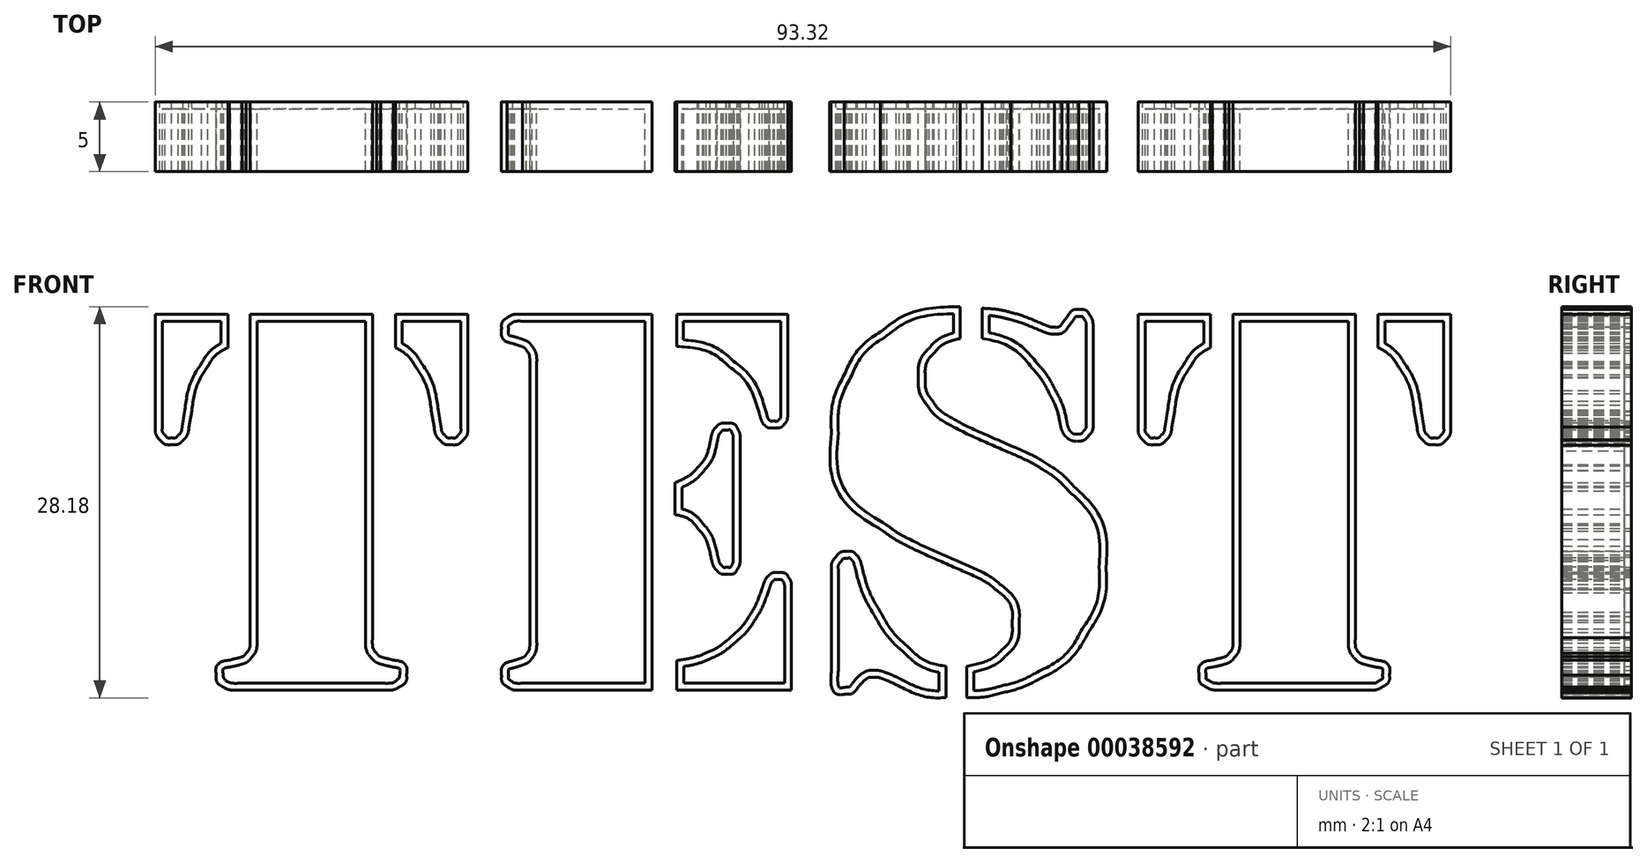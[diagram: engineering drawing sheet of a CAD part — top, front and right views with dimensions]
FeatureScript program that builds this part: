
annotation { "Feature Type Name" : "Feature", "Feature Type Description" : "" }
export const myFeature = defineFeature(function(context is Context, id is Id, definition is map)
    precondition{}
    {
        {
            var Q0;
            Q0=qCreatedBy(makeId("Front.planeOp"),FACE);
            var sketch = newSketch(context, id + "F0", { "sketchPlane" : qUnion([Q0])});
            skLineSegment(sketch, "E0", {"start": v(-31.02, 13.54) * mm, "end": v(-31.02, -9.77) * mm});
            skFitSpline(sketch, "E1", {"points": [v(-31.02, -9.77) * mm, v(-31.02, -10.29) * mm, v(-30.92, -10.66) * mm, v(-30.72, -10.88) * mm]});
            skFitSpline(sketch, "E2", {"points": [v(-30.72, -10.88) * mm, v(-30.61, -11.02) * mm, v(-30.51, -11.1) * mm, v(-30.42, -11.13) * mm]});
            skFitSpline(sketch, "E3", {"points": [v(-30.42, -11.13) * mm, v(-30.33, -11.17) * mm, v(-30.02, -11.25) * mm, v(-29.5, -11.38) * mm]});
            skFitSpline(sketch, "E4", {"points": [v(-29.5, -11.38) * mm, v(-28.87, -11.53) * mm, v(-28.56, -11.89) * mm, v(-28.56, -12.47) * mm]});
            skFitSpline(sketch, "E5", {"points": [v(-28.56, -12.47) * mm, v(-28.56, -12.82) * mm, v(-28.73, -13.1) * mm, v(-29.07, -13.3) * mm]});
            skFitSpline(sketch, "E6", {"points": [v(-29.07, -13.3) * mm, v(-29.32, -13.46) * mm, v(-29.75, -13.54) * mm, v(-30.34, -13.54) * mm]});
            skLineSegment(sketch, "E7", {"start": v(-30.34, -13.54) * mm, "end": v(-31, -13.54) * mm});
            skLineSegment(sketch, "E8", {"start": v(-31, -13.54) * mm, "end": v(-39.85, -13.54) * mm});
            skLineSegment(sketch, "E9", {"start": v(-39.85, -13.54) * mm, "end": v(-40.5, -13.54) * mm});
            skFitSpline(sketch, "E10", {"points": [v(-40.5, -13.54) * mm, v(-41.08, -13.54) * mm, v(-41.52, -13.45) * mm, v(-41.82, -13.28) * mm]});
            skFitSpline(sketch, "E11", {"points": [v(-41.82, -13.28) * mm, v(-42.12, -13.1) * mm, v(-42.27, -12.83) * mm, v(-42.27, -12.47) * mm]});
            skFitSpline(sketch, "E12", {"points": [v(-42.27, -12.47) * mm, v(-42.27, -11.89) * mm, v(-41.95, -11.53) * mm, v(-41.31, -11.38) * mm]});
            skFitSpline(sketch, "E13", {"points": [v(-41.31, -11.38) * mm, v(-40.8, -11.25) * mm, v(-40.5, -11.17) * mm, v(-40.4, -11.13) * mm]});
            skFitSpline(sketch, "E14", {"points": [v(-40.4, -11.13) * mm, v(-40.3, -11.1) * mm, v(-40.22, -11.02) * mm, v(-40.12, -10.88) * mm]});
            skFitSpline(sketch, "E15", {"points": [v(-40.12, -10.88) * mm, v(-39.93, -10.66) * mm, v(-39.83, -10.29) * mm, v(-39.83, -9.77) * mm]});
            skLineSegment(sketch, "E16", {"start": v(-39.83, -9.77) * mm, "end": v(-39.83, 13.54) * mm});
            skLineSegment(sketch, "E17", {"start": v(-39.83, 13.54) * mm, "end": v(-31.02, 13.54) * mm});
            skLineSegment(sketch, "E18", {"start": v(-24.15, 13.54) * mm, "end": v(-24.15, 5.43) * mm});
            skFitSpline(sketch, "E19", {"points": [v(-24.15, 5.43) * mm, v(-24.15, 5.04) * mm, v(-24.26, 4.73) * mm, v(-24.48, 4.5) * mm]});
            skFitSpline(sketch, "E20", {"points": [v(-24.48, 4.5) * mm, v(-24.7, 4.26) * mm, v(-24.98, 4.14) * mm, v(-25.32, 4.14) * mm]});
            skFitSpline(sketch, "E21", {"points": [v(-25.32, 4.14) * mm, v(-25.65, 4.14) * mm, v(-25.93, 4.25) * mm, v(-26.14, 4.46) * mm]});
            skFitSpline(sketch, "E22", {"points": [v(-26.14, 4.46) * mm, v(-26.36, 4.68) * mm, v(-26.5, 4.98) * mm, v(-26.57, 5.37) * mm]});
            skLineSegment(sketch, "E23", {"start": v(-26.57, 5.37) * mm, "end": v(-26.77, 6.58) * mm});
            skFitSpline(sketch, "E24", {"points": [v(-26.77, 6.58) * mm, v(-26.97, 7.8) * mm, v(-27.35, 8.87) * mm, v(-27.92, 9.77) * mm]});
            skFitSpline(sketch, "E25", {"points": [v(-27.92, 9.77) * mm, v(-28.28, 10.33) * mm, v(-28.76, 10.79) * mm, v(-29.37, 11.14) * mm]});
            skLineSegment(sketch, "E26", {"start": v(-29.37, 11.14) * mm, "end": v(-29.37, 13.54) * mm});
            skLineSegment(sketch, "E27", {"start": v(-29.37, 13.54) * mm, "end": v(-24.15, 13.54) * mm});
            skLineSegment(sketch, "E28", {"start": v(-46.65, 13.54) * mm, "end": v(-41.43, 13.54) * mm});
            skLineSegment(sketch, "E29", {"start": v(-41.43, 13.54) * mm, "end": v(-41.43, 11.14) * mm});
            skFitSpline(sketch, "E30", {"points": [v(-41.43, 11.14) * mm, v(-42.06, 10.79) * mm, v(-42.54, 10.33) * mm, v(-42.88, 9.77) * mm]});
            skFitSpline(sketch, "E31", {"points": [v(-42.88, 9.77) * mm, v(-43.45, 8.87) * mm, v(-43.83, 7.8) * mm, v(-44.03, 6.58) * mm]});
            skLineSegment(sketch, "E32", {"start": v(-44.03, 6.58) * mm, "end": v(-44.23, 5.37) * mm});
            skFitSpline(sketch, "E33", {"points": [v(-44.23, 5.37) * mm, v(-44.3, 4.98) * mm, v(-44.44, 4.68) * mm, v(-44.66, 4.46) * mm]});
            skFitSpline(sketch, "E34", {"points": [v(-44.66, 4.46) * mm, v(-44.88, 4.25) * mm, v(-45.15, 4.14) * mm, v(-45.48, 4.14) * mm]});
            skFitSpline(sketch, "E35", {"points": [v(-45.48, 4.14) * mm, v(-45.83, 4.14) * mm, v(-46.1, 4.26) * mm, v(-46.33, 4.5) * mm]});
            skFitSpline(sketch, "E36", {"points": [v(-46.33, 4.5) * mm, v(-46.54, 4.73) * mm, v(-46.65, 5.04) * mm, v(-46.65, 5.43) * mm]});
            skLineSegment(sketch, "E37", {"start": v(-46.65, 5.43) * mm, "end": v(-46.65, 13.54) * mm});
            skLineSegment(sketch, "E38", {"start": v(-10.87, 13.54) * mm, "end": v(-10.87, -13.54) * mm});
            skLineSegment(sketch, "E39", {"start": v(-10.87, -13.54) * mm, "end": v(-19.7, -13.54) * mm});
            skLineSegment(sketch, "E40", {"start": v(-19.7, -13.54) * mm, "end": v(-20.22, -13.54) * mm});
            skFitSpline(sketch, "E41", {"points": [v(-20.22, -13.54) * mm, v(-20.7, -13.54) * mm, v(-21.06, -13.45) * mm, v(-21.32, -13.28) * mm]});
            skFitSpline(sketch, "E42", {"points": [v(-21.32, -13.28) * mm, v(-21.58, -13.1) * mm, v(-21.7, -12.84) * mm, v(-21.7, -12.51) * mm]});
            skFitSpline(sketch, "E43", {"points": [v(-21.7, -12.51) * mm, v(-21.7, -11.97) * mm, v(-21.44, -11.61) * mm, v(-20.92, -11.44) * mm]});
            skFitSpline(sketch, "E44", {"points": [v(-20.92, -11.44) * mm, v(-20.48, -11.3) * mm, v(-20.22, -11.2) * mm, v(-20.15, -11.17) * mm]});
            skFitSpline(sketch, "E45", {"points": [v(-20.15, -11.17) * mm, v(-20.08, -11.14) * mm, v(-20, -11.06) * mm, v(-19.92, -10.94) * mm]});
            skFitSpline(sketch, "E46", {"points": [v(-19.92, -10.94) * mm, v(-19.76, -10.73) * mm, v(-19.69, -10.4) * mm, v(-19.68, -9.93) * mm]});
            skLineSegment(sketch, "E47", {"start": v(-19.68, -9.93) * mm, "end": v(-19.68, 9.93) * mm});
            skFitSpline(sketch, "E48", {"points": [v(-19.68, 9.93) * mm, v(-19.69, 10.4) * mm, v(-19.76, 10.73) * mm, v(-19.92, 10.94) * mm]});
            skFitSpline(sketch, "E49", {"points": [v(-19.92, 10.94) * mm, v(-20, 11.06) * mm, v(-20.08, 11.14) * mm, v(-20.15, 11.17) * mm]});
            skFitSpline(sketch, "E50", {"points": [v(-20.15, 11.17) * mm, v(-20.22, 11.2) * mm, v(-20.48, 11.3) * mm, v(-20.92, 11.44) * mm]});
            skFitSpline(sketch, "E51", {"points": [v(-20.92, 11.44) * mm, v(-21.44, 11.61) * mm, v(-21.7, 11.97) * mm, v(-21.7, 12.51) * mm]});
            skFitSpline(sketch, "E52", {"points": [v(-21.7, 12.51) * mm, v(-21.7, 12.84) * mm, v(-21.58, 13.1) * mm, v(-21.32, 13.28) * mm]});
            skFitSpline(sketch, "E53", {"points": [v(-21.32, 13.28) * mm, v(-21.06, 13.45) * mm, v(-20.7, 13.54) * mm, v(-20.22, 13.54) * mm]});
            skLineSegment(sketch, "E54", {"start": v(-20.22, 13.54) * mm, "end": v(-19.7, 13.54) * mm});
            skLineSegment(sketch, "E55", {"start": v(-19.7, 13.54) * mm, "end": v(-10.87, 13.54) * mm});
            skLineSegment(sketch, "E56", {"start": v(-9.1, 13.54) * mm, "end": v(-1.11, 13.54) * mm});
            skLineSegment(sketch, "E57", {"start": v(-1.11, 13.54) * mm, "end": v(-1.11, 6.52) * mm});
            skFitSpline(sketch, "E58", {"points": [v(-1.11, 6.52) * mm, v(-1.11, 6.1) * mm, v(-1.2, 5.81) * mm, v(-1.35, 5.63) * mm]});
            skFitSpline(sketch, "E59", {"points": [v(-1.35, 5.63) * mm, v(-1.5, 5.44) * mm, v(-1.76, 5.35) * mm, v(-2.1, 5.35) * mm]});
            skFitSpline(sketch, "E60", {"points": [v(-2.1, 5.35) * mm, v(-2.4, 5.35) * mm, v(-2.6, 5.4) * mm, v(-2.74, 5.53) * mm]});
            skFitSpline(sketch, "E61", {"points": [v(-2.74, 5.53) * mm, v(-2.87, 5.65) * mm, v(-3, 5.9) * mm, v(-3.12, 6.26) * mm]});
            skFitSpline(sketch, "E62", {"points": [v(-3.12, 6.26) * mm, v(-3.62, 7.8) * mm, v(-4.36, 8.97) * mm, v(-5.33, 9.77) * mm]});
            skFitSpline(sketch, "E63", {"points": [v(-5.33, 9.77) * mm, v(-6.3, 10.58) * mm, v(-7.56, 11.06) * mm, v(-9.1, 11.22) * mm]});
            skLineSegment(sketch, "E64", {"start": v(-9.1, 11.22) * mm, "end": v(-9.1, 13.54) * mm});
            skLineSegment(sketch, "E65", {"start": v(-9.2, -0.9) * mm, "end": v(-9.2, 1.4) * mm});
            skFitSpline(sketch, "E66", {"points": [v(-9.2, 1.4) * mm, v(-8.44, 1.77) * mm, v(-7.87, 2.17) * mm, v(-7.5, 2.6) * mm]});
            skFitSpline(sketch, "E67", {"points": [v(-7.5, 2.6) * mm, v(-7.13, 3.05) * mm, v(-6.86, 3.63) * mm, v(-6.69, 4.36) * mm]});
            skFitSpline(sketch, "E68", {"points": [v(-6.69, 4.36) * mm, v(-6.58, 4.86) * mm, v(-6.44, 5.2) * mm, v(-6.27, 5.4) * mm]});
            skFitSpline(sketch, "E69", {"points": [v(-6.27, 5.4) * mm, v(-6.1, 5.59) * mm, v(-5.85, 5.69) * mm, v(-5.54, 5.69) * mm]});
            skFitSpline(sketch, "E70", {"points": [v(-5.54, 5.69) * mm, v(-5.11, 5.69) * mm, v(-4.82, 5.52) * mm, v(-4.66, 5.19) * mm]});
            skFitSpline(sketch, "E71", {"points": [v(-4.66, 5.19) * mm, v(-4.57, 5.02) * mm, v(-4.52, 4.63) * mm, v(-4.52, 4.02) * mm]});
            skLineSegment(sketch, "E72", {"start": v(-4.52, 4.02) * mm, "end": v(-4.52, -3.54) * mm});
            skFitSpline(sketch, "E73", {"points": [v(-4.52, -3.54) * mm, v(-4.52, -4.16) * mm, v(-4.6, -4.6) * mm, v(-4.73, -4.83) * mm]});
            skFitSpline(sketch, "E74", {"points": [v(-4.73, -4.83) * mm, v(-4.87, -5.07) * mm, v(-5.13, -5.19) * mm, v(-5.5, -5.19) * mm]});
            skFitSpline(sketch, "E75", {"points": [v(-5.5, -5.19) * mm, v(-5.8, -5.19) * mm, v(-6.04, -5.1) * mm, v(-6.21, -4.91) * mm]});
            skFitSpline(sketch, "E76", {"points": [v(-6.21, -4.91) * mm, v(-6.38, -4.73) * mm, v(-6.52, -4.42) * mm, v(-6.63, -3.98) * mm]});
            skFitSpline(sketch, "E77", {"points": [v(-6.63, -3.98) * mm, v(-6.85, -3.07) * mm, v(-7.17, -2.36) * mm, v(-7.6, -1.88) * mm]});
            skFitSpline(sketch, "E78", {"points": [v(-7.6, -1.88) * mm, v(-8, -1.39) * mm, v(-8.55, -1.06) * mm, v(-9.2, -0.9) * mm]});
            skLineSegment(sketch, "E79", {"start": v(-9.09, -13.54) * mm, "end": v(-9.09, -11.4) * mm});
            skFitSpline(sketch, "E80", {"points": [v(-9.09, -11.4) * mm, v(-8.23, -11.27) * mm, v(-7.52, -11.08) * mm, v(-6.96, -10.84) * mm]});
            skFitSpline(sketch, "E81", {"points": [v(-6.96, -10.84) * mm, v(-6.4, -10.6) * mm, v(-5.83, -10.24) * mm, v(-5.26, -9.75) * mm]});
            skFitSpline(sketch, "E82", {"points": [v(-5.26, -9.75) * mm, v(-4.69, -9.26) * mm, v(-4.24, -8.76) * mm, v(-3.9, -8.24) * mm]});
            skFitSpline(sketch, "E83", {"points": [v(-3.9, -8.24) * mm, v(-3.56, -7.71) * mm, v(-3.24, -7.02) * mm, v(-2.94, -6.16) * mm]});
            skFitSpline(sketch, "E84", {"points": [v(-2.94, -6.16) * mm, v(-2.8, -5.74) * mm, v(-2.64, -5.45) * mm, v(-2.48, -5.3) * mm]});
            skFitSpline(sketch, "E85", {"points": [v(-2.48, -5.3) * mm, v(-2.32, -5.15) * mm, v(-2.1, -5.07) * mm, v(-1.83, -5.07) * mm]});
            skFitSpline(sketch, "E86", {"points": [v(-1.83, -5.07) * mm, v(-1.46, -5.07) * mm, v(-1.2, -5.18) * mm, v(-1.05, -5.4) * mm]});
            skFitSpline(sketch, "E87", {"points": [v(-1.05, -5.4) * mm, v(-0.9, -5.62) * mm, v(-0.83, -6) * mm, v(-0.83, -6.54) * mm]});
            skLineSegment(sketch, "E88", {"start": v(-0.83, -6.54) * mm, "end": v(-0.83, -13.54) * mm});
            skLineSegment(sketch, "E89", {"start": v(-0.83, -13.54) * mm, "end": v(-9.09, -13.54) * mm});
            skLineSegment(sketch, "E90", {"start": v(11.33, 14.08) * mm, "end": v(11.33, 11.8) * mm});
            skFitSpline(sketch, "E91", {"points": [v(11.33, 11.8) * mm, v(10.51, 11.57) * mm, v(9.89, 11.22) * mm, v(9.46, 10.76) * mm]});
            skFitSpline(sketch, "E92", {"points": [v(9.46, 10.76) * mm, v(9.03, 10.29) * mm, v(8.81, 9.7) * mm, v(8.81, 9.02) * mm]});
            skFitSpline(sketch, "E93", {"points": [v(8.81, 9.02) * mm, v(8.81, 8.36) * mm, v(8.99, 7.78) * mm, v(9.35, 7.28) * mm]});
            skFitSpline(sketch, "E94", {"points": [v(9.35, 7.28) * mm, v(9.7, 6.79) * mm, v(10.29, 6.31) * mm, v(11.1, 5.86) * mm]});
            skFitSpline(sketch, "E95", {"points": [v(11.1, 5.86) * mm, v(11.65, 5.56) * mm, v(12.9, 4.98) * mm, v(14.86, 4.12) * mm]});
            skFitSpline(sketch, "E96", {"points": [v(14.86, 4.12) * mm, v(16.05, 3.6) * mm, v(16.98, 3.14) * mm, v(17.63, 2.72) * mm]});
            skFitSpline(sketch, "E97", {"points": [v(17.63, 2.72) * mm, v(18.29, 2.3) * mm, v(18.9, 1.78) * mm, v(19.49, 1.16) * mm]});
            skFitSpline(sketch, "E98", {"points": [v(19.49, 1.16) * mm, v(21.05, -0.48) * mm, v(21.83, -2.43) * mm, v(21.83, -4.7) * mm]});
            skFitSpline(sketch, "E99", {"points": [v(21.83, -4.7) * mm, v(21.83, -6.4) * mm, v(21.4, -7.96) * mm, v(20.56, -9.38) * mm]});
            skFitSpline(sketch, "E100", {"points": [v(20.56, -9.38) * mm, v(19.71, -10.8) * mm, v(18.55, -11.9) * mm, v(17.07, -12.7) * mm]});
            skFitSpline(sketch, "E101", {"points": [v(17.07, -12.7) * mm, v(16.27, -13.13) * mm, v(15.4, -13.47) * mm, v(14.46, -13.71) * mm]});
            skFitSpline(sketch, "E102", {"points": [v(14.46, -13.71) * mm, v(13.51, -13.96) * mm, v(12.63, -14.08) * mm, v(11.8, -14.08) * mm]});
            skLineSegment(sketch, "E103", {"start": v(11.8, -14.08) * mm, "end": v(11.8, -11.82) * mm});
            skFitSpline(sketch, "E104", {"points": [v(11.8, -11.82) * mm, v(12.96, -11.54) * mm, v(13.79, -11.15) * mm, v(14.3, -10.66) * mm]});
            skFitSpline(sketch, "E105", {"points": [v(14.3, -10.66) * mm, v(14.8, -10.16) * mm, v(15.06, -9.49) * mm, v(15.06, -8.64) * mm]});
            skFitSpline(sketch, "E106", {"points": [v(15.06, -8.64) * mm, v(15.06, -7.76) * mm, v(14.66, -6.98) * mm, v(13.87, -6.3) * mm]});
            skFitSpline(sketch, "E107", {"points": [v(13.87, -6.3) * mm, v(13.34, -5.86) * mm, v(12.34, -5.32) * mm, v(10.85, -4.67) * mm]});
            skFitSpline(sketch, "E108", {"points": [v(10.85, -4.67) * mm, v(9.23, -3.96) * mm, v(8.11, -3.45) * mm, v(7.51, -3.15) * mm]});
            skFitSpline(sketch, "E109", {"points": [v(7.51, -3.15) * mm, v(6.9, -2.84) * mm, v(6.33, -2.48) * mm, v(5.77, -2.07) * mm]});
            skFitSpline(sketch, "E110", {"points": [v(5.77, -2.07) * mm, v(3.29, -0.3) * mm, v(2.04, 2.06) * mm, v(2.04, 5.01) * mm]});
            skFitSpline(sketch, "E111", {"points": [v(2.04, 5.01) * mm, v(2.04, 6.52) * mm, v(2.35, 7.91) * mm, v(2.98, 9.19) * mm]});
            skFitSpline(sketch, "E112", {"points": [v(2.98, 9.19) * mm, v(3.6, 10.46) * mm, v(4.46, 11.5) * mm, v(5.58, 12.27) * mm]});
            skFitSpline(sketch, "E113", {"points": [v(5.58, 12.27) * mm, v(7.12, 13.36) * mm, v(9.04, 13.96) * mm, v(11.33, 14.08) * mm]});
            skLineSegment(sketch, "E114", {"start": v(12.9, 11.8) * mm, "end": v(12.9, 13.98) * mm});
            skFitSpline(sketch, "E115", {"points": [v(12.9, 13.98) * mm, v(13.7, 13.93) * mm, v(14.38, 13.82) * mm, v(14.96, 13.67) * mm]});
            skFitSpline(sketch, "E116", {"points": [v(14.96, 13.67) * mm, v(15.54, 13.52) * mm, v(16.37, 13.22) * mm, v(17.44, 12.77) * mm]});
            skFitSpline(sketch, "E117", {"points": [v(17.44, 12.77) * mm, v(17.7, 12.66) * mm, v(17.93, 12.61) * mm, v(18.1, 12.61) * mm]});
            skFitSpline(sketch, "E118", {"points": [v(18.1, 12.61) * mm, v(18.35, 12.61) * mm, v(18.53, 12.7) * mm, v(18.65, 12.87) * mm]});
            skLineSegment(sketch, "E119", {"start": v(18.65, 12.87) * mm, "end": v(19.09, 13.44) * mm});
            skFitSpline(sketch, "E120", {"points": [v(19.09, 13.44) * mm, v(19.3, 13.74) * mm, v(19.56, 13.88) * mm, v(19.86, 13.88) * mm]});
            skFitSpline(sketch, "E121", {"points": [v(19.86, 13.88) * mm, v(20.22, 13.88) * mm, v(20.48, 13.75) * mm, v(20.65, 13.5) * mm]});
            skFitSpline(sketch, "E122", {"points": [v(20.65, 13.5) * mm, v(20.81, 13.24) * mm, v(20.9, 12.83) * mm, v(20.9, 12.27) * mm]});
            skLineSegment(sketch, "E123", {"start": v(20.9, 12.27) * mm, "end": v(20.9, 5.72) * mm});
            skFitSpline(sketch, "E124", {"points": [v(20.9, 5.72) * mm, v(20.9, 5.34) * mm, v(20.79, 5.03) * mm, v(20.57, 4.78) * mm]});
            skFitSpline(sketch, "E125", {"points": [v(20.57, 4.78) * mm, v(20.35, 4.54) * mm, v(20.07, 4.42) * mm, v(19.72, 4.42) * mm]});
            skFitSpline(sketch, "E126", {"points": [v(19.72, 4.42) * mm, v(19.46, 4.42) * mm, v(19.22, 4.5) * mm, v(19, 4.67) * mm]});
            skFitSpline(sketch, "E127", {"points": [v(19, 4.67) * mm, v(18.87, 4.78) * mm, v(18.78, 4.9) * mm, v(18.7, 5.06) * mm]});
            skFitSpline(sketch, "E128", {"points": [v(18.7, 5.06) * mm, v(18.63, 5.21) * mm, v(18.56, 5.47) * mm, v(18.5, 5.82) * mm]});
            skFitSpline(sketch, "E129", {"points": [v(18.5, 5.82) * mm, v(18.35, 6.47) * mm, v(18.1, 7.14) * mm, v(17.74, 7.83) * mm]});
            skFitSpline(sketch, "E130", {"points": [v(17.74, 7.83) * mm, v(17.38, 8.52) * mm, v(16.97, 9.13) * mm, v(16.5, 9.67) * mm]});
            skFitSpline(sketch, "E131", {"points": [v(16.5, 9.67) * mm, v(15.54, 10.75) * mm, v(14.34, 11.45) * mm, v(12.9, 11.8) * mm]});
            skLineSegment(sketch, "E132", {"start": v(10.3, -11.82) * mm, "end": v(10.3, -14.08) * mm});
            skFitSpline(sketch, "E133", {"points": [v(10.3, -14.08) * mm, v(9.21, -14.08) * mm, v(8.02, -13.77) * mm, v(6.7, -13.15) * mm]});
            skFitSpline(sketch, "E134", {"points": [v(6.7, -13.15) * mm, v(6.22, -12.92) * mm, v(5.88, -12.78) * mm, v(5.7, -12.7) * mm]});
            skFitSpline(sketch, "E135", {"points": [v(5.7, -12.7) * mm, v(5.5, -12.64) * mm, v(5.33, -12.61) * mm, v(5.16, -12.61) * mm]});
            skFitSpline(sketch, "E136", {"points": [v(5.16, -12.61) * mm, v(4.9, -12.61) * mm, v(4.7, -12.65) * mm, v(4.56, -12.74) * mm]});
            skFitSpline(sketch, "E137", {"points": [v(4.56, -12.74) * mm, v(4.43, -12.83) * mm, v(4.22, -13.04) * mm, v(3.93, -13.38) * mm]});
            skFitSpline(sketch, "E138", {"points": [v(3.93, -13.38) * mm, v(3.7, -13.68) * mm, v(3.43, -13.82) * mm, v(3.16, -13.82) * mm]});
            skFitSpline(sketch, "E139", {"points": [v(3.16, -13.82) * mm, v(2.41, -13.82) * mm, v(2.04, -13.25) * mm, v(2.04, -12.11) * mm]});
            skLineSegment(sketch, "E140", {"start": v(2.04, -12.11) * mm, "end": v(2.04, -4.9) * mm});
            skFitSpline(sketch, "E141", {"points": [v(2.04, -4.9) * mm, v(2.04, -4.52) * mm, v(2.15, -4.2) * mm, v(2.36, -3.95) * mm]});
            skFitSpline(sketch, "E142", {"points": [v(2.36, -3.95) * mm, v(2.57, -3.7) * mm, v(2.84, -3.56) * mm, v(3.16, -3.54) * mm]});
            skFitSpline(sketch, "E143", {"points": [v(3.16, -3.54) * mm, v(3.45, -3.53) * mm, v(3.67, -3.61) * mm, v(3.84, -3.8) * mm]});
            skFitSpline(sketch, "E144", {"points": [v(3.84, -3.8) * mm, v(4, -3.97) * mm, v(4.15, -4.28) * mm, v(4.27, -4.73) * mm]});
            skFitSpline(sketch, "E145", {"points": [v(4.27, -4.73) * mm, v(4.57, -5.87) * mm, v(5.01, -6.94) * mm, v(5.59, -7.93) * mm]});
            skFitSpline(sketch, "E146", {"points": [v(5.59, -7.93) * mm, v(6.16, -8.92) * mm, v(6.83, -9.76) * mm, v(7.6, -10.45) * mm]});
            skFitSpline(sketch, "E147", {"points": [v(7.6, -10.45) * mm, v(8.38, -11.16) * mm, v(9.28, -11.62) * mm, v(10.3, -11.82) * mm]});
            skLineSegment(sketch, "E148", {"start": v(39.79, 13.54) * mm, "end": v(39.79, -9.77) * mm});
            skFitSpline(sketch, "E149", {"points": [v(39.79, -9.77) * mm, v(39.79, -10.29) * mm, v(39.89, -10.66) * mm, v(40.08, -10.88) * mm]});
            skFitSpline(sketch, "E150", {"points": [v(40.08, -10.88) * mm, v(40.2, -11.02) * mm, v(40.29, -11.1) * mm, v(40.38, -11.13) * mm]});
            skFitSpline(sketch, "E151", {"points": [v(40.38, -11.13) * mm, v(40.47, -11.17) * mm, v(40.78, -11.25) * mm, v(41.3, -11.38) * mm]});
            skFitSpline(sketch, "E152", {"points": [v(41.3, -11.38) * mm, v(41.93, -11.53) * mm, v(42.25, -11.89) * mm, v(42.25, -12.47) * mm]});
            skFitSpline(sketch, "E153", {"points": [v(42.25, -12.47) * mm, v(42.25, -12.82) * mm, v(42.08, -13.1) * mm, v(41.73, -13.3) * mm]});
            skFitSpline(sketch, "E154", {"points": [v(41.73, -13.3) * mm, v(41.48, -13.46) * mm, v(41.06, -13.54) * mm, v(40.46, -13.54) * mm]});
            skLineSegment(sketch, "E155", {"start": v(40.46, -13.54) * mm, "end": v(39.8, -13.54) * mm});
            skLineSegment(sketch, "E156", {"start": v(39.8, -13.54) * mm, "end": v(30.96, -13.54) * mm});
            skLineSegment(sketch, "E157", {"start": v(30.96, -13.54) * mm, "end": v(30.3, -13.54) * mm});
            skFitSpline(sketch, "E158", {"points": [v(30.3, -13.54) * mm, v(29.72, -13.54) * mm, v(29.28, -13.45) * mm, v(28.98, -13.28) * mm]});
            skFitSpline(sketch, "E159", {"points": [v(28.98, -13.28) * mm, v(28.68, -13.1) * mm, v(28.54, -12.83) * mm, v(28.54, -12.47) * mm]});
            skFitSpline(sketch, "E160", {"points": [v(28.54, -12.47) * mm, v(28.54, -11.89) * mm, v(28.85, -11.53) * mm, v(29.49, -11.38) * mm]});
            skFitSpline(sketch, "E161", {"points": [v(29.49, -11.38) * mm, v(30, -11.25) * mm, v(30.3, -11.17) * mm, v(30.4, -11.13) * mm]});
            skFitSpline(sketch, "E162", {"points": [v(30.4, -11.13) * mm, v(30.5, -11.1) * mm, v(30.59, -11.02) * mm, v(30.68, -10.88) * mm]});
            skFitSpline(sketch, "E163", {"points": [v(30.68, -10.88) * mm, v(30.88, -10.66) * mm, v(30.98, -10.29) * mm, v(30.98, -9.77) * mm]});
            skLineSegment(sketch, "E164", {"start": v(30.98, -9.77) * mm, "end": v(30.98, 13.54) * mm});
            skLineSegment(sketch, "E165", {"start": v(30.98, 13.54) * mm, "end": v(39.79, 13.54) * mm});
            skLineSegment(sketch, "E166", {"start": v(46.65, 13.54) * mm, "end": v(46.65, 5.43) * mm});
            skFitSpline(sketch, "E167", {"points": [v(46.65, 5.43) * mm, v(46.65, 5.04) * mm, v(46.54, 4.73) * mm, v(46.33, 4.5) * mm]});
            skFitSpline(sketch, "E168", {"points": [v(46.33, 4.5) * mm, v(46.1, 4.26) * mm, v(45.83, 4.14) * mm, v(45.48, 4.14) * mm]});
            skFitSpline(sketch, "E169", {"points": [v(45.48, 4.14) * mm, v(45.15, 4.14) * mm, v(44.88, 4.25) * mm, v(44.66, 4.46) * mm]});
            skFitSpline(sketch, "E170", {"points": [v(44.66, 4.46) * mm, v(44.44, 4.68) * mm, v(44.3, 4.98) * mm, v(44.23, 5.37) * mm]});
            skLineSegment(sketch, "E171", {"start": v(44.23, 5.37) * mm, "end": v(44.03, 6.58) * mm});
            skFitSpline(sketch, "E172", {"points": [v(44.03, 6.58) * mm, v(43.83, 7.8) * mm, v(43.45, 8.87) * mm, v(42.88, 9.77) * mm]});
            skFitSpline(sketch, "E173", {"points": [v(42.88, 9.77) * mm, v(42.53, 10.33) * mm, v(42.04, 10.79) * mm, v(41.43, 11.14) * mm]});
            skLineSegment(sketch, "E174", {"start": v(41.43, 11.14) * mm, "end": v(41.43, 13.54) * mm});
            skLineSegment(sketch, "E175", {"start": v(41.43, 13.54) * mm, "end": v(46.65, 13.54) * mm});
            skLineSegment(sketch, "E176", {"start": v(24.15, 13.54) * mm, "end": v(29.37, 13.54) * mm});
            skLineSegment(sketch, "E177", {"start": v(29.37, 13.54) * mm, "end": v(29.37, 11.14) * mm});
            skFitSpline(sketch, "E178", {"points": [v(29.37, 11.14) * mm, v(28.75, 10.79) * mm, v(28.26, 10.33) * mm, v(27.92, 9.77) * mm]});
            skFitSpline(sketch, "E179", {"points": [v(27.92, 9.77) * mm, v(27.35, 8.87) * mm, v(26.97, 7.8) * mm, v(26.77, 6.58) * mm]});
            skLineSegment(sketch, "E180", {"start": v(26.77, 6.58) * mm, "end": v(26.57, 5.37) * mm});
            skFitSpline(sketch, "E181", {"points": [v(26.57, 5.37) * mm, v(26.5, 4.98) * mm, v(26.36, 4.68) * mm, v(26.14, 4.46) * mm]});
            skFitSpline(sketch, "E182", {"points": [v(26.14, 4.46) * mm, v(25.93, 4.25) * mm, v(25.65, 4.14) * mm, v(25.32, 4.14) * mm]});
            skFitSpline(sketch, "E183", {"points": [v(25.32, 4.14) * mm, v(24.98, 4.14) * mm, v(24.7, 4.26) * mm, v(24.48, 4.5) * mm]});
            skFitSpline(sketch, "E184", {"points": [v(24.48, 4.5) * mm, v(24.26, 4.73) * mm, v(24.15, 5.04) * mm, v(24.15, 5.43) * mm]});
            skLineSegment(sketch, "E185", {"start": v(24.15, 5.43) * mm, "end": v(24.15, 13.54) * mm});
            skSolve(sketch);
        }
        {
            var Q0;
            Q0=qSketchRegion(id+"F0",true);
            extrude(context, id + "F1", {"entities" : qUnion([Q0]), "depth" : 5 * mm});
        }
        {
            var Q0;
            Q0=makeQuery(id+"F1.opExtrude","CAP_FACE",FACE,{"disambiguationData":[OSD([sQuery(id+"F0.wireOp",EDGE,"E28"),sQuery(id+"F0.wireOp",EDGE,"E29"),sQuery(id+"F0.wireOp",EDGE,"E30"),sQuery(id+"F0.wireOp",EDGE,"E31"),sQuery(id+"F0.wireOp",EDGE,"E32"),sQuery(id+"F0.wireOp",EDGE,"E33"),sQuery(id+"F0.wireOp",EDGE,"E34"),sQuery(id+"F0.wireOp",EDGE,"E35"),sQuery(id+"F0.wireOp",EDGE,"E36"),sQuery(id+"F0.wireOp",EDGE,"E37")])],"isStart":false});
            var Q1;
            Q1=makeQuery(id+"F1.opExtrude","CAP_FACE",FACE,{"disambiguationData":[OSD([sQuery(id+"F0.wireOp",EDGE,"E18"),sQuery(id+"F0.wireOp",EDGE,"E19"),sQuery(id+"F0.wireOp",EDGE,"E20"),sQuery(id+"F0.wireOp",EDGE,"E21"),sQuery(id+"F0.wireOp",EDGE,"E22"),sQuery(id+"F0.wireOp",EDGE,"E23"),sQuery(id+"F0.wireOp",EDGE,"E24"),sQuery(id+"F0.wireOp",EDGE,"E25"),sQuery(id+"F0.wireOp",EDGE,"E26"),sQuery(id+"F0.wireOp",EDGE,"E27")])],"isStart":false});
            var Q2;
            Q2=makeQuery(id+"F1.opExtrude","CAP_FACE",FACE,{"disambiguationData":[OSD([sQuery(id+"F0.wireOp",EDGE,"E38"),sQuery(id+"F0.wireOp",EDGE,"E39"),sQuery(id+"F0.wireOp",EDGE,"E40"),sQuery(id+"F0.wireOp",EDGE,"E41"),sQuery(id+"F0.wireOp",EDGE,"E42"),sQuery(id+"F0.wireOp",EDGE,"E43"),sQuery(id+"F0.wireOp",EDGE,"E44"),sQuery(id+"F0.wireOp",EDGE,"E45"),sQuery(id+"F0.wireOp",EDGE,"E46"),sQuery(id+"F0.wireOp",EDGE,"E47"),sQuery(id+"F0.wireOp",EDGE,"E48"),sQuery(id+"F0.wireOp",EDGE,"E49"),sQuery(id+"F0.wireOp",EDGE,"E50"),sQuery(id+"F0.wireOp",EDGE,"E51"),sQuery(id+"F0.wireOp",EDGE,"E52"),sQuery(id+"F0.wireOp",EDGE,"E53"),sQuery(id+"F0.wireOp",EDGE,"E54"),sQuery(id+"F0.wireOp",EDGE,"E55")])],"isStart":false});
            var Q3;
            Q3=makeQuery(id+"F1.opExtrude","CAP_FACE",FACE,{"disambiguationData":[OSD([sQuery(id+"F0.wireOp",EDGE,"E56"),sQuery(id+"F0.wireOp",EDGE,"E57"),sQuery(id+"F0.wireOp",EDGE,"E58"),sQuery(id+"F0.wireOp",EDGE,"E59"),sQuery(id+"F0.wireOp",EDGE,"E60"),sQuery(id+"F0.wireOp",EDGE,"E61"),sQuery(id+"F0.wireOp",EDGE,"E62"),sQuery(id+"F0.wireOp",EDGE,"E63"),sQuery(id+"F0.wireOp",EDGE,"E64")])],"isStart":false});
            var Q4;
            Q4=makeQuery(id+"F1.opExtrude","CAP_FACE",FACE,{"disambiguationData":[OSD([sQuery(id+"F0.wireOp",EDGE,"E65"),sQuery(id+"F0.wireOp",EDGE,"E66"),sQuery(id+"F0.wireOp",EDGE,"E67"),sQuery(id+"F0.wireOp",EDGE,"E68"),sQuery(id+"F0.wireOp",EDGE,"E69"),sQuery(id+"F0.wireOp",EDGE,"E70"),sQuery(id+"F0.wireOp",EDGE,"E71"),sQuery(id+"F0.wireOp",EDGE,"E72"),sQuery(id+"F0.wireOp",EDGE,"E73"),sQuery(id+"F0.wireOp",EDGE,"E74"),sQuery(id+"F0.wireOp",EDGE,"E75"),sQuery(id+"F0.wireOp",EDGE,"E76"),sQuery(id+"F0.wireOp",EDGE,"E77"),sQuery(id+"F0.wireOp",EDGE,"E78")])],"isStart":false});
            var Q5;
            Q5=makeQuery(id+"F1.opExtrude","CAP_FACE",FACE,{"disambiguationData":[OSD([sQuery(id+"F0.wireOp",EDGE,"E79"),sQuery(id+"F0.wireOp",EDGE,"E80"),sQuery(id+"F0.wireOp",EDGE,"E81"),sQuery(id+"F0.wireOp",EDGE,"E82"),sQuery(id+"F0.wireOp",EDGE,"E83"),sQuery(id+"F0.wireOp",EDGE,"E84"),sQuery(id+"F0.wireOp",EDGE,"E85"),sQuery(id+"F0.wireOp",EDGE,"E86"),sQuery(id+"F0.wireOp",EDGE,"E87"),sQuery(id+"F0.wireOp",EDGE,"E88"),sQuery(id+"F0.wireOp",EDGE,"E89")])],"isStart":false});
            var Q6;
            Q6=makeQuery(id+"F1.opExtrude","CAP_FACE",FACE,{"disambiguationData":[OSD([sQuery(id+"F0.wireOp",EDGE,"E132"),sQuery(id+"F0.wireOp",EDGE,"E133"),sQuery(id+"F0.wireOp",EDGE,"E134"),sQuery(id+"F0.wireOp",EDGE,"E135"),sQuery(id+"F0.wireOp",EDGE,"E136"),sQuery(id+"F0.wireOp",EDGE,"E137"),sQuery(id+"F0.wireOp",EDGE,"E138"),sQuery(id+"F0.wireOp",EDGE,"E139"),sQuery(id+"F0.wireOp",EDGE,"E140"),sQuery(id+"F0.wireOp",EDGE,"E141"),sQuery(id+"F0.wireOp",EDGE,"E142"),sQuery(id+"F0.wireOp",EDGE,"E143"),sQuery(id+"F0.wireOp",EDGE,"E144"),sQuery(id+"F0.wireOp",EDGE,"E145"),sQuery(id+"F0.wireOp",EDGE,"E146"),sQuery(id+"F0.wireOp",EDGE,"E147")])],"isStart":false});
            var Q7;
            Q7=makeQuery(id+"F1.opExtrude","CAP_FACE",FACE,{"disambiguationData":[OSD([sQuery(id+"F0.wireOp",EDGE,"E90"),sQuery(id+"F0.wireOp",EDGE,"E91"),sQuery(id+"F0.wireOp",EDGE,"E92"),sQuery(id+"F0.wireOp",EDGE,"E93"),sQuery(id+"F0.wireOp",EDGE,"E94"),sQuery(id+"F0.wireOp",EDGE,"E95"),sQuery(id+"F0.wireOp",EDGE,"E96"),sQuery(id+"F0.wireOp",EDGE,"E97"),sQuery(id+"F0.wireOp",EDGE,"E98"),sQuery(id+"F0.wireOp",EDGE,"E99"),sQuery(id+"F0.wireOp",EDGE,"E100"),sQuery(id+"F0.wireOp",EDGE,"E101"),sQuery(id+"F0.wireOp",EDGE,"E102"),sQuery(id+"F0.wireOp",EDGE,"E103"),sQuery(id+"F0.wireOp",EDGE,"E104"),sQuery(id+"F0.wireOp",EDGE,"E105"),sQuery(id+"F0.wireOp",EDGE,"E106"),sQuery(id+"F0.wireOp",EDGE,"E107"),sQuery(id+"F0.wireOp",EDGE,"E108"),sQuery(id+"F0.wireOp",EDGE,"E109"),sQuery(id+"F0.wireOp",EDGE,"E110"),sQuery(id+"F0.wireOp",EDGE,"E111"),sQuery(id+"F0.wireOp",EDGE,"E112"),sQuery(id+"F0.wireOp",EDGE,"E113")])],"isStart":false});
            var Q8;
            Q8=makeQuery(id+"F1.opExtrude","CAP_FACE",FACE,{"disambiguationData":[OSD([sQuery(id+"F0.wireOp",EDGE,"E114"),sQuery(id+"F0.wireOp",EDGE,"E115"),sQuery(id+"F0.wireOp",EDGE,"E116"),sQuery(id+"F0.wireOp",EDGE,"E117"),sQuery(id+"F0.wireOp",EDGE,"E118"),sQuery(id+"F0.wireOp",EDGE,"E119"),sQuery(id+"F0.wireOp",EDGE,"E120"),sQuery(id+"F0.wireOp",EDGE,"E121"),sQuery(id+"F0.wireOp",EDGE,"E122"),sQuery(id+"F0.wireOp",EDGE,"E123"),sQuery(id+"F0.wireOp",EDGE,"E124"),sQuery(id+"F0.wireOp",EDGE,"E125"),sQuery(id+"F0.wireOp",EDGE,"E126"),sQuery(id+"F0.wireOp",EDGE,"E127"),sQuery(id+"F0.wireOp",EDGE,"E128"),sQuery(id+"F0.wireOp",EDGE,"E129"),sQuery(id+"F0.wireOp",EDGE,"E130"),sQuery(id+"F0.wireOp",EDGE,"E131")])],"isStart":false});
            var Q9;
            Q9=makeQuery(id+"F1.opExtrude","CAP_FACE",FACE,{"disambiguationData":[OSD([sQuery(id+"F0.wireOp",EDGE,"E176"),sQuery(id+"F0.wireOp",EDGE,"E177"),sQuery(id+"F0.wireOp",EDGE,"E178"),sQuery(id+"F0.wireOp",EDGE,"E179"),sQuery(id+"F0.wireOp",EDGE,"E180"),sQuery(id+"F0.wireOp",EDGE,"E181"),sQuery(id+"F0.wireOp",EDGE,"E182"),sQuery(id+"F0.wireOp",EDGE,"E183"),sQuery(id+"F0.wireOp",EDGE,"E184"),sQuery(id+"F0.wireOp",EDGE,"E185")])],"isStart":false});
            var Q10;
            Q10=makeQuery(id+"F1.opExtrude","CAP_FACE",FACE,{"disambiguationData":[OSD([sQuery(id+"F0.wireOp",EDGE,"E148"),sQuery(id+"F0.wireOp",EDGE,"E149"),sQuery(id+"F0.wireOp",EDGE,"E150"),sQuery(id+"F0.wireOp",EDGE,"E151"),sQuery(id+"F0.wireOp",EDGE,"E152"),sQuery(id+"F0.wireOp",EDGE,"E153"),sQuery(id+"F0.wireOp",EDGE,"E154"),sQuery(id+"F0.wireOp",EDGE,"E155"),sQuery(id+"F0.wireOp",EDGE,"E156"),sQuery(id+"F0.wireOp",EDGE,"E157"),sQuery(id+"F0.wireOp",EDGE,"E158"),sQuery(id+"F0.wireOp",EDGE,"E159"),sQuery(id+"F0.wireOp",EDGE,"E160"),sQuery(id+"F0.wireOp",EDGE,"E161"),sQuery(id+"F0.wireOp",EDGE,"E162"),sQuery(id+"F0.wireOp",EDGE,"E163"),sQuery(id+"F0.wireOp",EDGE,"E164"),sQuery(id+"F0.wireOp",EDGE,"E165")])],"isStart":false});
            var Q11;
            Q11=makeQuery(id+"F1.opExtrude","CAP_FACE",FACE,{"disambiguationData":[OSD([sQuery(id+"F0.wireOp",EDGE,"E166"),sQuery(id+"F0.wireOp",EDGE,"E167"),sQuery(id+"F0.wireOp",EDGE,"E168"),sQuery(id+"F0.wireOp",EDGE,"E169"),sQuery(id+"F0.wireOp",EDGE,"E170"),sQuery(id+"F0.wireOp",EDGE,"E171"),sQuery(id+"F0.wireOp",EDGE,"E172"),sQuery(id+"F0.wireOp",EDGE,"E173"),sQuery(id+"F0.wireOp",EDGE,"E174"),sQuery(id+"F0.wireOp",EDGE,"E175")])],"isStart":false});
            var Q12;
            Q12=makeQuery(id+"F1.opExtrude","CAP_FACE",FACE,{"disambiguationData":[OSD([sQuery(id+"F0.wireOp",EDGE,"E0"),sQuery(id+"F0.wireOp",EDGE,"E1"),sQuery(id+"F0.wireOp",EDGE,"E2"),sQuery(id+"F0.wireOp",EDGE,"E3"),sQuery(id+"F0.wireOp",EDGE,"E4"),sQuery(id+"F0.wireOp",EDGE,"E5"),sQuery(id+"F0.wireOp",EDGE,"E6"),sQuery(id+"F0.wireOp",EDGE,"E7"),sQuery(id+"F0.wireOp",EDGE,"E8"),sQuery(id+"F0.wireOp",EDGE,"E9"),sQuery(id+"F0.wireOp",EDGE,"E10"),sQuery(id+"F0.wireOp",EDGE,"E11"),sQuery(id+"F0.wireOp",EDGE,"E12"),sQuery(id+"F0.wireOp",EDGE,"E13"),sQuery(id+"F0.wireOp",EDGE,"E14"),sQuery(id+"F0.wireOp",EDGE,"E15"),sQuery(id+"F0.wireOp",EDGE,"E16"),sQuery(id+"F0.wireOp",EDGE,"E17")])],"isStart":false});
            shell(context, id + "F2", {"entities" : qUnion([Q0, Q1, Q2, Q3, Q4, Q5, Q6, Q7, Q8, Q9, Q10, Q11, Q12]), "thickness" : .5 * mm});
        }
    });
